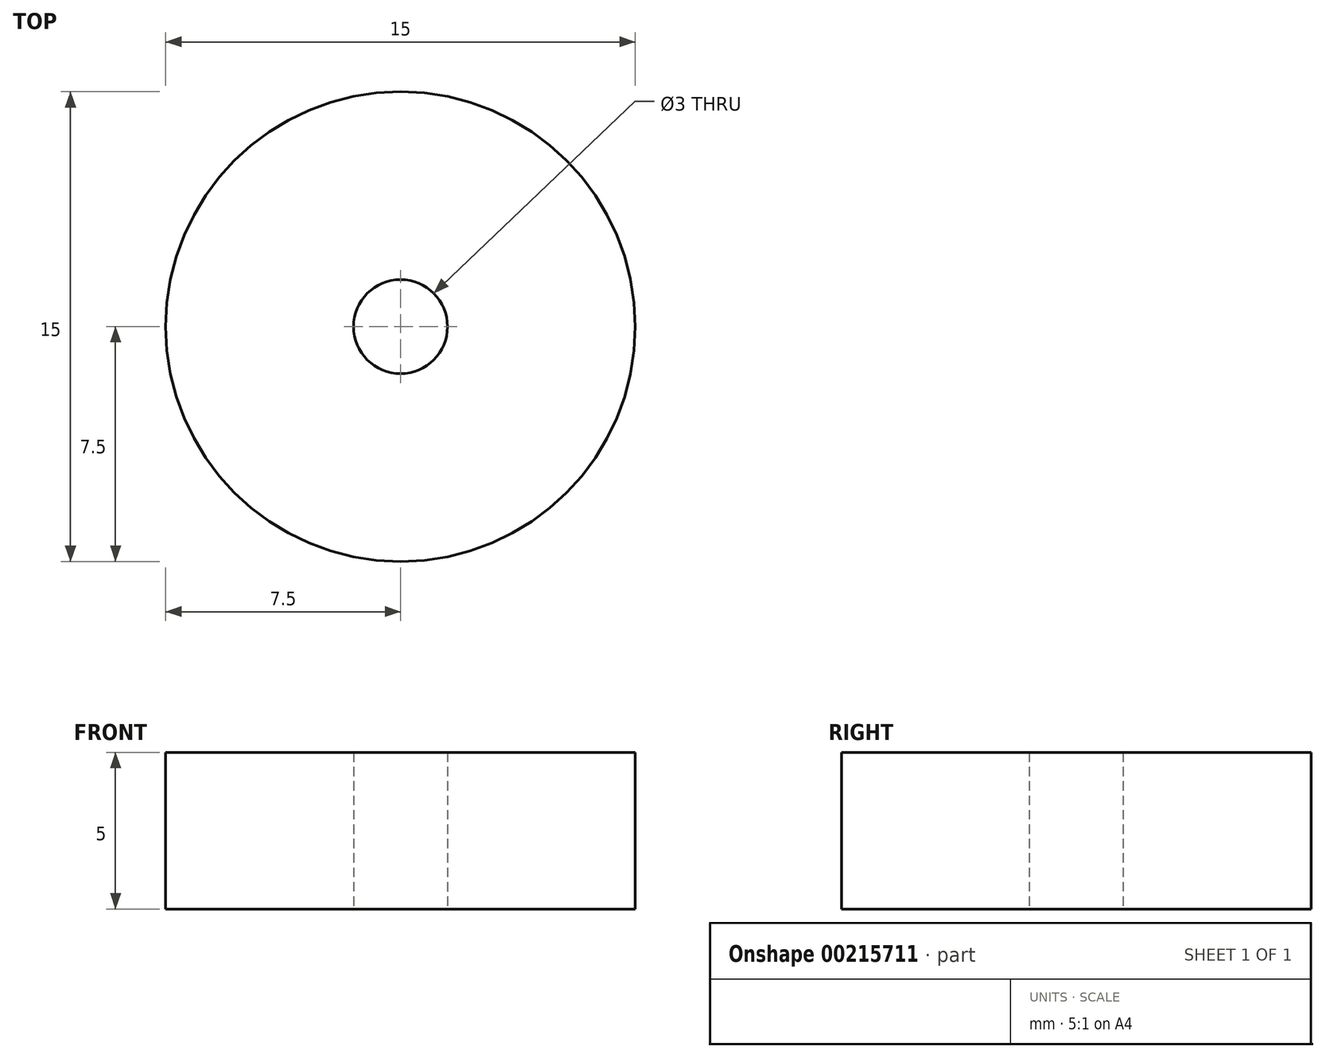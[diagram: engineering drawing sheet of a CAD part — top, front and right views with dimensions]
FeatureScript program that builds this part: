
annotation { "Feature Type Name" : "Feature", "Feature Type Description" : "" }
export const myFeature = defineFeature(function(context is Context, id is Id, definition is map)
    precondition{}
    {
        {
            var Q0;
            Q0=qCreatedBy(makeId("Top.planeOp"),FACE);
            var sketch = newSketch(context, id + "F0", { "sketchPlane" : qUnion([Q0])});
            skCircle(sketch, "E0", {"center": v(0, 0) * mm, "radius": 7.5 * mm});
            skCircle(sketch, "E1", {"center": v(0, 0) * mm, "radius": 1.5 * mm});
            skSolve(sketch);
        }
        {
            var Q0;
            Q0 = qSketchRegion(id + "F0", true);
            extrude(context, id + "F1", {"entities" : qUnion([Q0]), "depth" : 5 * mm});
        }
    });
